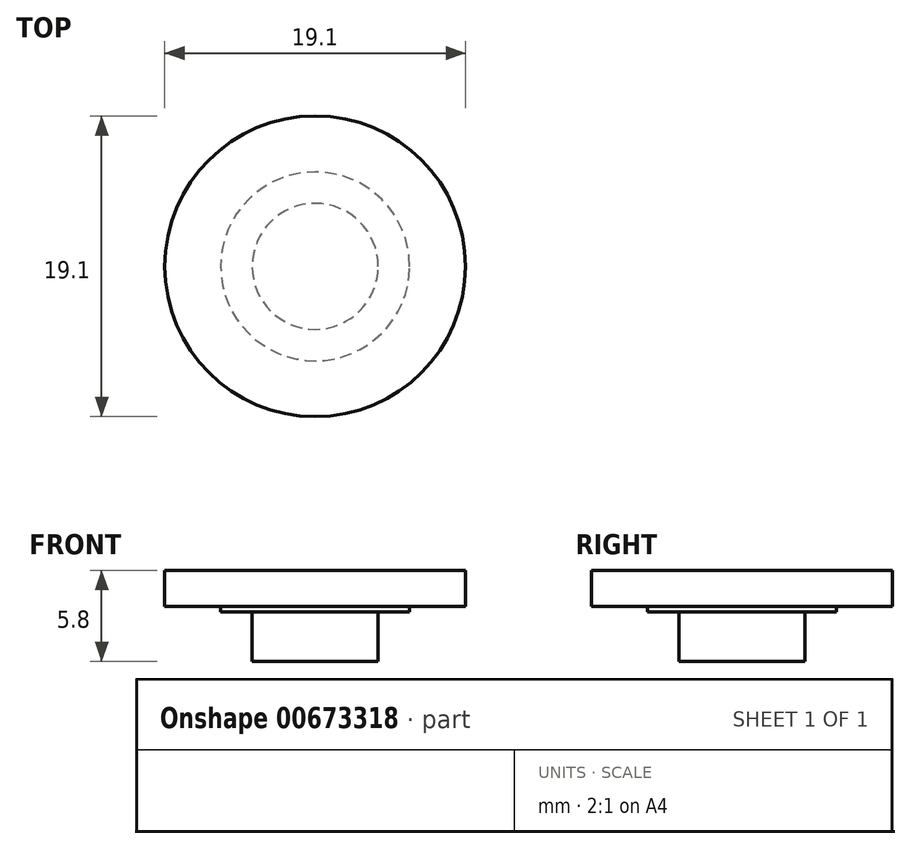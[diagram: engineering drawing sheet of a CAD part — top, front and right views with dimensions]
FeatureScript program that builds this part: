
annotation { "Feature Type Name" : "Feature", "Feature Type Description" : "" }
export const myFeature = defineFeature(function(context is Context, id is Id, definition is map)
    precondition{}
    {
        {
            var Q0;
            Q0=qCreatedBy(makeId("Top.planeOp"),FACE);
            var sketch = newSketch(context, id + "F0", { "sketchPlane" : qUnion([Q0])});
            skCircle(sketch, "E0", {"center": v(0, 0) * mm, "radius": 9.55 * mm});
            skCircle(sketch, "E1", {"center": v(0, 0) * mm, "radius": 6 * mm});
            skCircle(sketch, "E2", {"center": v(0, 0) * mm, "radius": 4 * mm});
            skSolve(sketch);
        }
        {
            var Q0;
            Q0=makeQuery(id+"F0.imprint","IMPRINT",FACE,{"disambiguationData":[TD([[makeQuery(id+"F0.imprint","IMPRINT",EDGE,{"derivedFrom":sQuery(id+"F0.wireOp",EDGE,"E0")}),1.0]])]});
            extrude(context, id + "F1", {"entities" : qUnion([Q0]), "oppositeDirection" : true, "depth" : 2.3 * mm, "offsetDistance" : 25 * mm});
        }
        {
            var Q0;
            Q0=makeQuery(id+"F0.imprint","IMPRINT",FACE,{"disambiguationData":[TD([[makeQuery(id+"F0.imprint","IMPRINT",EDGE,{"derivedFrom":sQuery(id+"F0.wireOp",EDGE,"E1")}),1.0]])]});
            extrude(context, id + "F2", {"entities" : qUnion([Q0]), "operationType" : NewBodyOperationType.ADD, "oppositeDirection" : true, "depth" : 2.65 * mm, "offsetDistance" : 25 * mm});
        }
        {
            var Q0;
            Q0=makeQuery(id+"F0.imprint","IMPRINT",FACE,{"disambiguationData":[TD([[makeQuery(id+"F0.imprint","IMPRINT",EDGE,{"derivedFrom":sQuery(id+"F0.wireOp",EDGE,"E2")}),1.0]])]});
            extrude(context, id + "F3", {"entities" : qUnion([Q0]), "operationType" : NewBodyOperationType.ADD, "oppositeDirection" : true, "depth" : 5.8 * mm, "offsetDistance" : 25 * mm});
        }
    });
